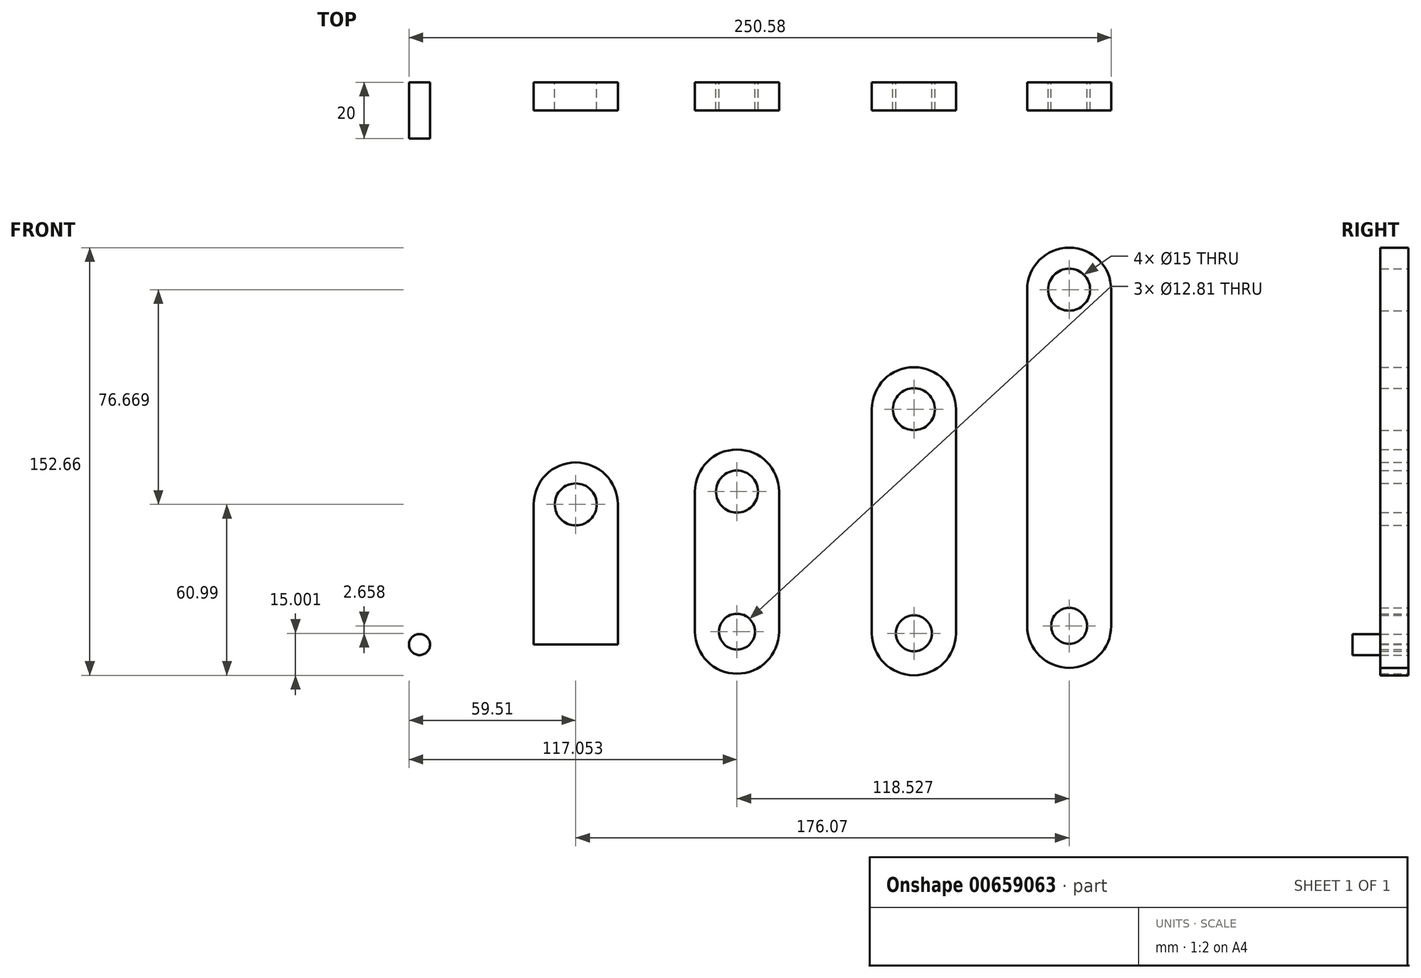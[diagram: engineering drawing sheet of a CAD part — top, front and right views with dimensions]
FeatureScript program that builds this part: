
annotation { "Feature Type Name" : "Feature", "Feature Type Description" : "" }
export const myFeature = defineFeature(function(context is Context, id is Id, definition is map)
    precondition{}
    {
        {
            assignVariable(context, id + "F0", {"name" : "thickness", "anyValue" : 10});
        }
        {
            var Q0;
            Q0=qCreatedBy(makeId("Front.planeOp"),FACE);
            var sketch = newSketch(context, id + "F1", { "sketchPlane" : qUnion([Q0])});
            skLineSegment(sketch, "E0", {"start": v(-15, 0) * mm, "end": v(0, 0) * mm});
            skLineSegment(sketch, "E1", {"start": v(-15, 0) * mm, "end": v(-15, 50) * mm});
            skLineSegment(sketch, "E2.MirrorCS", {"start": v(15, 0) * mm, "end": v(0, 0) * mm});
            skLineSegment(sketch, "E3.MirrorCS", {"start": v(15, 0) * mm, "end": v(15, 50) * mm});
            skCircle(sketch, "E4", {"center": v(0, 50) * mm, "radius": 15 * mm});
            skCircle(sketch, "E5", {"center": v(0, 50) * mm, "radius": 7.5 * mm});
            skSolve(sketch);
        }
        {
            var Q0;
            Q0=makeQuery(id+"F1.imprint","IMPRINT",FACE,{"disambiguationData":[TD([[makeQuery(id+"F1.imprint","IMPRINT",EDGE,{"derivedFrom":sQuery(id+"F1.wireOp",EDGE,"E0")}),1.0]])]});
            var Q1;
            Q1=makeQuery(id+"F1.imprint","IMPRINT",FACE,{"disambiguationData":[TD([[makeQuery(id+"F1.imprint","IMPRINT",EDGE,{"derivedFrom":sQuery(id+"F1.wireOp",EDGE,"E5")}),-1.0]])]});
            extrude(context, id + "F2", {"entities" : qUnion([Q0, Q1]), "depth" : (getVariable(context, 'thickness')) * mm, "offsetDistance" : 25 * mm});
        }
        {
            var Q0;
            Q0=qCreatedBy(makeId("Front.planeOp"),FACE);
            var sketch = newSketch(context, id + "F3", { "sketchPlane" : qUnion([Q0])});
            skLineSegment(sketch, "E6", {"start": v(42.54, 4.6) * mm, "end": v(42.54, 54.6) * mm});
            skLineSegment(sketch, "E7.MirrorCS", {"start": v(72.54, 4.6) * mm, "end": v(72.54, 54.6) * mm});
            skCircle(sketch, "E8", {"center": v(57.54, 54.6) * mm, "radius": 15 * mm});
            skCircle(sketch, "E9", {"center": v(57.54, 54.6) * mm, "radius": 7.5 * mm});
            skCircle(sketch, "E10", {"center": v(57.54, 4.6) * mm, "radius": 15 * mm});
            skCircle(sketch, "E11", {"center": v(57.54, 4.6) * mm, "radius": 6.4 * mm});
            skSolve(sketch);
        }
        {
            var Q0;
            {var subQ0=sQuery(id+"F3.wireOp",EDGE,"E6");Q0=makeQuery(id+"F3.imprint","IMPRINT",FACE,{"disambiguationData":[TD([[makeQuery(id+"F3.imprint","IMPRINT",EDGE,{"derivedFrom":subQ0}),-1.0]])]});}
            var Q1;
            Q1=makeQuery(id+"F3.imprint","IMPRINT",FACE,{"disambiguationData":[TD([[makeQuery(id+"F3.imprint","IMPRINT",EDGE,{"derivedFrom":sQuery(id+"F3.wireOp",EDGE,"E9")}),-1.0]])]});
            var Q2;
            Q2=makeQuery(id+"F3.imprint","IMPRINT",FACE,{"disambiguationData":[TD([[makeQuery(id+"F3.imprint","IMPRINT",EDGE,{"derivedFrom":sQuery(id+"F3.wireOp",EDGE,"E11")}),-1.0]])]});
            extrude(context, id + "F4", {"entities" : qUnion([Q0, Q1, Q2]), "depth" : (getVariable(context, 'thickness')) * mm, "offsetDistance" : 25 * mm});
        }
        {
            var Q0;
            Q0=qCreatedBy(makeId("Front.planeOp"),FACE);
            var sketch = newSketch(context, id + "F5", { "sketchPlane" : qUnion([Q0])});
            skLineSegment(sketch, "E12", {"start": v(105.67, 4.01) * mm, "end": v(105.67, 84.01) * mm});
            skLineSegment(sketch, "E13.MirrorCS", {"start": v(135.67, 4.01) * mm, "end": v(135.67, 84.01) * mm});
            skCircle(sketch, "E14", {"center": v(120.67, 84.01) * mm, "radius": 15 * mm});
            skCircle(sketch, "E15", {"center": v(120.67, 84.01) * mm, "radius": 7.5 * mm});
            skCircle(sketch, "E16", {"center": v(120.67, 4.01) * mm, "radius": 15 * mm});
            skCircle(sketch, "E17", {"center": v(120.67, 4.01) * mm, "radius": 6.4 * mm});
            skSolve(sketch);
        }
        {
            var Q0;
            {var subQ0=sQuery(id+"F5.wireOp",EDGE,"E12");Q0=makeQuery(id+"F5.imprint","IMPRINT",FACE,{"disambiguationData":[TD([[makeQuery(id+"F5.imprint","IMPRINT",EDGE,{"derivedFrom":subQ0}),-1.0]])]});}
            var Q1;
            Q1=makeQuery(id+"F5.imprint","IMPRINT",FACE,{"disambiguationData":[TD([[makeQuery(id+"F5.imprint","IMPRINT",EDGE,{"derivedFrom":sQuery(id+"F5.wireOp",EDGE,"E15")}),-1.0]])]});
            var Q2;
            Q2=makeQuery(id+"F5.imprint","IMPRINT",FACE,{"disambiguationData":[TD([[makeQuery(id+"F5.imprint","IMPRINT",EDGE,{"derivedFrom":sQuery(id+"F5.wireOp",EDGE,"E17")}),-1.0]])]});
            extrude(context, id + "F6", {"entities" : qUnion([Q0, Q1, Q2]), "depth" : (getVariable(context, 'thickness')) * mm, "offsetDistance" : 25 * mm});
        }
        {
            var Q0;
            Q0=qCreatedBy(makeId("Front.planeOp"),FACE);
            var sketch = newSketch(context, id + "F7", { "sketchPlane" : qUnion([Q0])});
            skLineSegment(sketch, "E18", {"start": v(161.07, 6.67) * mm, "end": v(161.07, 126.67) * mm});
            skLineSegment(sketch, "E19.MirrorCS", {"start": v(191.07, 6.67) * mm, "end": v(191.07, 126.67) * mm});
            skCircle(sketch, "E20", {"center": v(176.07, 126.67) * mm, "radius": 15 * mm});
            skCircle(sketch, "E21", {"center": v(176.07, 126.67) * mm, "radius": 7.5 * mm});
            skCircle(sketch, "E22", {"center": v(176.07, 6.67) * mm, "radius": 15 * mm});
            skCircle(sketch, "E23", {"center": v(176.07, 6.67) * mm, "radius": 6.4 * mm});
            skSolve(sketch);
        }
        {
            var Q0;
            Q0=makeQuery(id+"F7.imprint","IMPRINT",FACE,{"disambiguationData":[TD([[makeQuery(id+"F7.imprint","IMPRINT",EDGE,{"derivedFrom":sQuery(id+"F7.wireOp",EDGE,"E21")}),-1.0]])]});
            var Q1;
            {var subQ0=sQuery(id+"F7.wireOp",EDGE,"E18");Q1=makeQuery(id+"F7.imprint","IMPRINT",FACE,{"disambiguationData":[TD([[makeQuery(id+"F7.imprint","IMPRINT",EDGE,{"derivedFrom":subQ0}),-1.0]])]});}
            var Q2;
            Q2=makeQuery(id+"F7.imprint","IMPRINT",FACE,{"disambiguationData":[TD([[makeQuery(id+"F7.imprint","IMPRINT",EDGE,{"derivedFrom":sQuery(id+"F7.wireOp",EDGE,"E23")}),-1.0]])]});
            extrude(context, id + "F8", {"entities" : qUnion([Q0, Q1, Q2]), "depth" : (getVariable(context, 'thickness')) * mm, "offsetDistance" : 25 * mm});
        }
        {
            var Q0;
            Q0=qCreatedBy(makeId("Front.planeOp"),FACE);
            var sketch = newSketch(context, id + "F9", { "sketchPlane" : qUnion([Q0])});
            skCircle(sketch, "E24", {"center": v(-55.76, 0) * mm, "radius": 3.75 * mm});
            skSolve(sketch);
        }
        {
            var Q0;
            Q0=makeQuery(id+"F9.imprint","IMPRINT",FACE,{"disambiguationData":[TD([[makeQuery(id+"F9.imprint","IMPRINT",EDGE,{"derivedFrom":sQuery(id+"F9.wireOp",EDGE,"E24")}),1.0]])]});
            extrude(context, id + "F10", {"entities" : qUnion([Q0]), "depth" : (getVariable(context, 'thickness') * 2) * mm, "offsetDistance" : 25 * mm});
        }
    });
